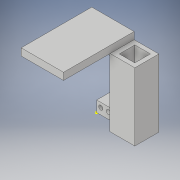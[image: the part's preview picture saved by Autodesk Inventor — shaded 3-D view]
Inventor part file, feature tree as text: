
AUTODESK INVENTOR PART (.ipt)
format: ipt  version: 2018.1 (Build 221171000, 171)  size: 203,264 bytes
history: native  units: in
note: dims shown in document units (in); Inventor stores cm internally (conversion verified against a paired STEP export)
features: sketch x15, extrude x13
ambient origin geometry x8: Origin, YZ Plane, XZ Plane, XY Plane, X Axis, Y Axis, Z Axis, Center Point
bodies: Solid1 (feature_tree)
feature tree (28):
  sketch  "Sketch1"  dims[d0=2.78in d1=2.4in]
  sketch  "Sketch2"  dims[d2=0.5in d3=0.0in d4=0.15in]
  extrude  "Extrusion1"  Depth=2.4in
  extrude  "Extrusion2"  Depth=0.15in
  extrude  "Extrusion3"  Depth=0.15in
  extrude  "Extrusion4"  Depth=1.5in
  extrude  "Extrusion5"  Depth=0.825in
  extrude  "Extrusion6"  Depth=0.5in TaperAngle=0.0deg
  extrude  "Extrusion7"  Depth=1.6in TaperAngle=0.0deg
  sketch  "Sketch9"  dims[d22=0.15in d23=0.15in]
  extrude  "Extrusion8"  Depth=0.15in
  extrude  "Extrusion9"  Depth=0.15in
  extrude  "Extrusion10"  Depth=1.0in TaperAngle=0.0deg
  extrude  "Extrusion11"  Depth=1.0in
  extrude  "Extrusion12"  Depth=0.55in
  extrude  "Extrusion13"  Depth=0.55in TaperAngle=0.0deg
  sketch  "Sketch3"  dims[d5=0.15in d6=0.15in d7=0.15in]
  sketch  "Sketch4"  dims[d8=0.5in d9=0.0in d10=1.5in]
  sketch  "Sketch5"  dims[d11=0.8in d12=0.0in d13=0.825in]
  sketch  "Sketch6"  dims[d14=1.6in d15=0.5in d16=0.0in]
  sketch  "Sketch7"  dims[d17=1.6in d18=0.8in d19=0.0in]
  sketch  "Sketch8"  dims[d20=0.15in d21=0.15in]
  sketch  "Sketch10"  dims[d24=0.5in d25=0.0in d26=1.0in d27=0.0in]
  sketch  "Sketch11"  dims[d28=0.8in d29=0.0in d30=1.0in]
  sketch  "Sketch12"  dims[d31=3.0in d32=0.0in d33=0.55in]
  sketch  "Sketch13"  dims[d34=0.55in d35=3.0in d36=0.0in]
  sketch  "Sketch14"  dims[d37=3.0in d38=0.0in]
  sketch  "Sketch15"  dims[d39=0.08in d40=3.0in d41=0.0in d42=1.5in d43=2.5in d44=0.25in d45=0.0in]
